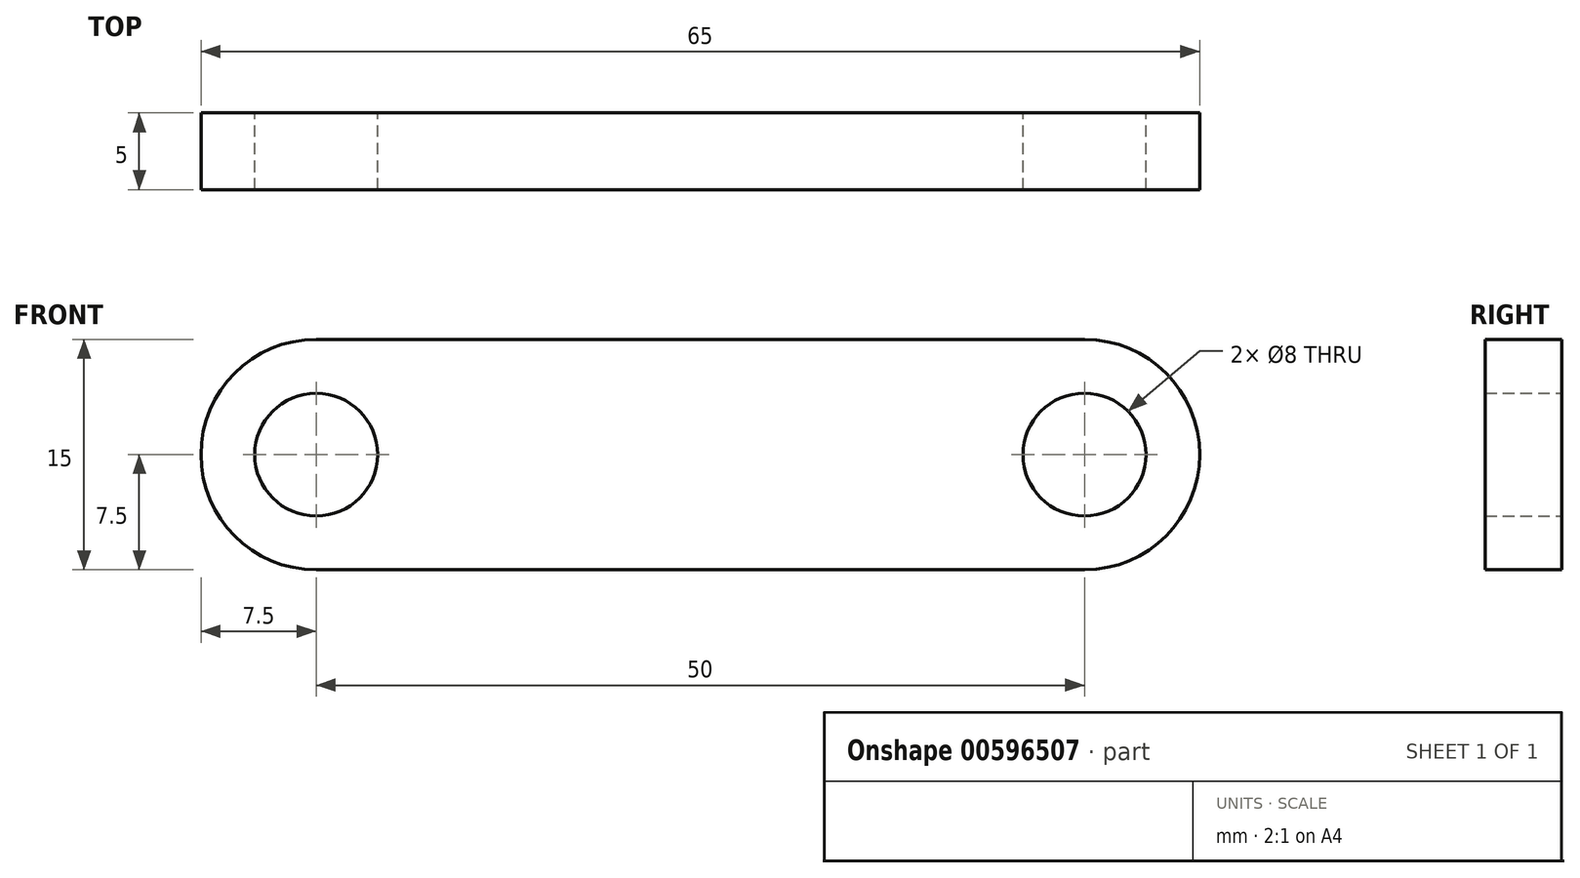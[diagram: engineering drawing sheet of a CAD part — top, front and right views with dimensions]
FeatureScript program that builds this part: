
annotation { "Feature Type Name" : "Feature", "Feature Type Description" : "" }
export const myFeature = defineFeature(function(context is Context, id is Id, definition is map)
    precondition{}
    {
        {
            var Q0;
            Q0=qCreatedBy(makeId("Front.planeOp"),FACE);
            var sketch = newSketch(context, id + "F0", { "sketchPlane" : qUnion([Q0])});
            skArc(sketch, "E0", {"start": v(0, 7.5) * mm, "mid": v(-7.5, 0) * mm, "end": v(0, -7.5) * mm});
            skArc(sketch, "E1", {"start": v(50, -7.5) * mm, "mid": v(57.5, 0) * mm, "end": v(50, 7.5) * mm});
            skCircle(sketch, "E2", {"center": v(0, 0) * mm, "radius": 4 * mm});
            skCircle(sketch, "E3", {"center": v(50, 0) * mm, "radius": 4 * mm});
            skLineSegment(sketch, "E4", {"start": v(0, 7.5) * mm, "end": v(50, 7.5) * mm});
            skLineSegment(sketch, "E5", {"start": v(50, -7.5) * mm, "end": v(0, -7.5) * mm});
            skSolve(sketch);
        }
        {
            var Q0;
            Q0=makeQuery(id+"F0.imprint","IMPRINT",FACE,{"disambiguationData":[TD([[makeQuery(id+"F0.imprint","IMPRINT",EDGE,{"derivedFrom":sQuery(id+"F0.wireOp",EDGE,"E0")}),1.0]])]});
            extrude(context, id + "F1", {"entities" : qUnion([Q0]), "depth" : 5 * mm, "offsetDistance" : 25 * mm});
        }
    });
